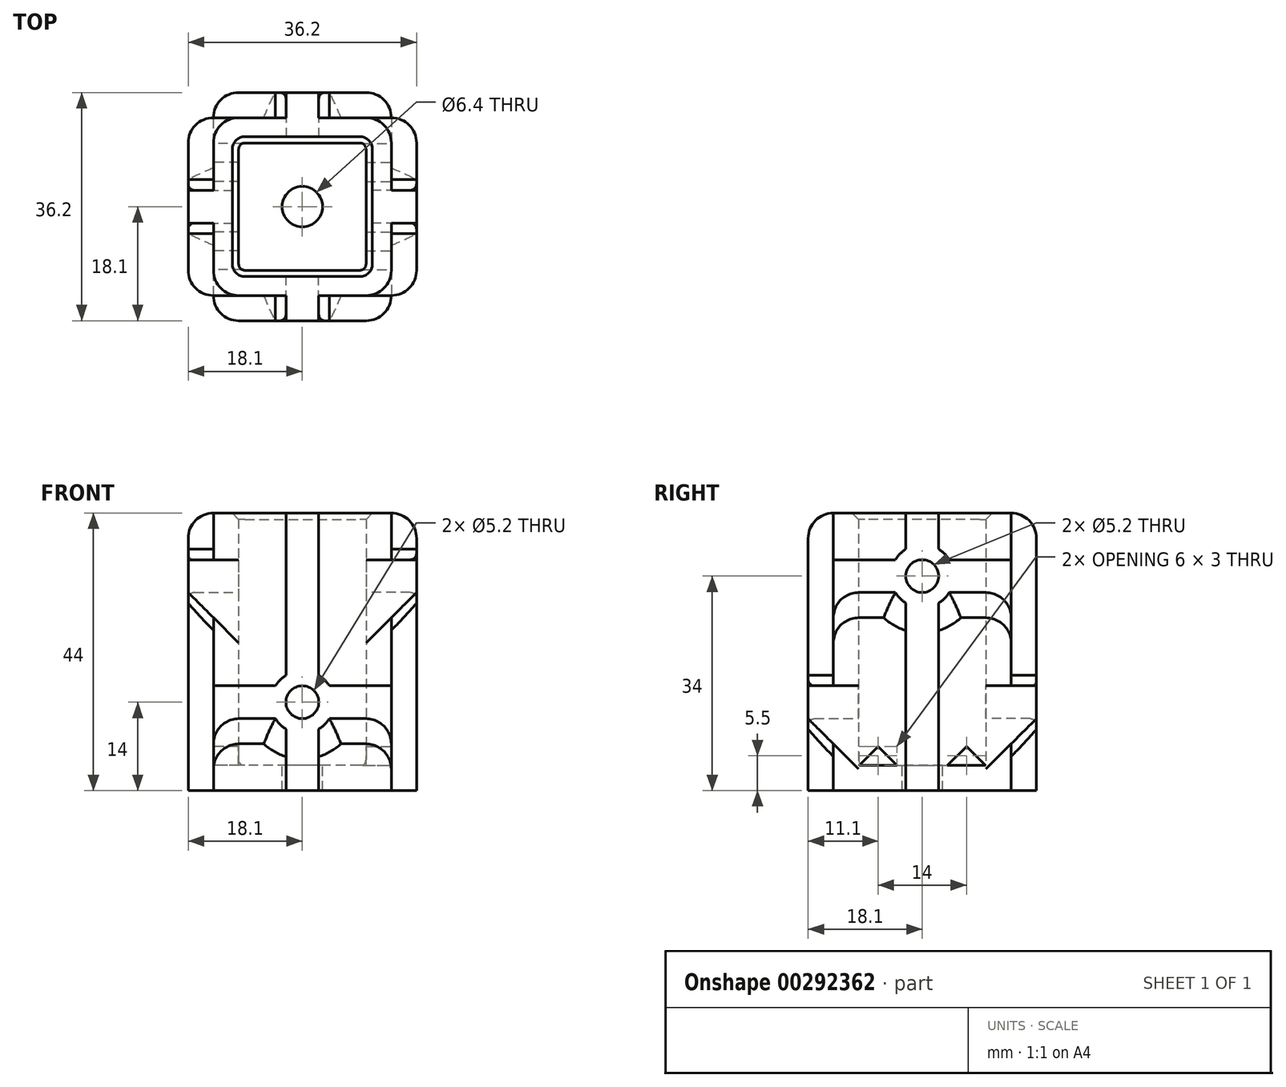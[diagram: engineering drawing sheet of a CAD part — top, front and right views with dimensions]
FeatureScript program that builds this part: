
annotation { "Feature Type Name" : "Feature", "Feature Type Description" : "" }
export const myFeature = defineFeature(function(context is Context, id is Id, definition is map)
    precondition{}
    {
        {
            var Q0;
            Q0=qCreatedBy(makeId("Top.planeOp"),FACE);
            var sketch = newSketch(context, id + "F0", { "sketchPlane" : qUnion([Q0])});
            skLineSegment(sketch, "E0.rect.bottom", {"start": v(10.1, -10.1) * mm, "end": v(-10.1, -10.1) * mm});
            skLineSegment(sketch, "E0.rect.top", {"start": v(10.1, 10.1) * mm, "end": v(-10.1, 10.1) * mm, "construction": true});
            skLineSegment(sketch, "E0.rect.left", {"start": v(10.1, -10.1) * mm, "end": v(10.1, 10.1) * mm, "construction": true});
            skLineSegment(sketch, "E0.rect.right", {"start": v(-10.1, -10.1) * mm, "end": v(-10.1, 10.1) * mm});
            skPoint(sketch, "E0.rect.middle", {"position": v(0, 0) * mm});
            skLineSegment(sketch, "E1.0", {"start": v(14.1, -14.1) * mm, "end": v(14.1, 14.1) * mm, "construction": true});
            skLineSegment(sketch, "E1.1", {"start": v(14.1, -14.1) * mm, "end": v(-14.1, -14.1) * mm});
            skLineSegment(sketch, "E1.2", {"start": v(-14.1, -14.1) * mm, "end": v(-14.1, 14.1) * mm});
            skLineSegment(sketch, "E1.3", {"start": v(14.1, 14.1) * mm, "end": v(-14.1, 14.1) * mm, "construction": true});
            skCircle(sketch, "E2", {"center": v(0, 0) * mm, "radius": 3.2 * mm});
            skLineSegment(sketch, "E3", {"start": v(-14.1, 14.1) * mm, "end": v(-2.26, 2.26) * mm});
            skLineSegment(sketch, "E4", {"start": v(2.26, -2.26) * mm, "end": v(14.1, -14.1) * mm});
            skSolve(sketch);
        }
        {
            var Q0;
            {var subQ5=sQuery(id+"F0.wireOp",EDGE,"E0.rect.right");Q0=makeQuery(id+"F0.imprint","IMPRINT",FACE,{"disambiguationData":[TD([[makeQuery(id+"F0.imprint","IMPRINT",EDGE,{"derivedFrom":subQ5}),1.0]])]});}
            extrude(context, id + "F1", {"entities" : qUnion([Q0]), "depth" : 40 * mm});
        }
        {
            var Q0;
            {var subQ3=sQuery(id+"F0.wireOp",EDGE,"E0.rect.bottom");Q0=makeQuery(id+"F0.imprint","IMPRINT",FACE,{"disambiguationData":[TD([[makeQuery(id+"F0.imprint","IMPRINT",EDGE,{"derivedFrom":subQ3}),1.0]])]});}
            var Q1;
            {var subQ0=sQuery(id+"F0.wireOp",EDGE,"E0.rect.bottom");Q1=makeQuery(id+"F0.imprint","IMPRINT",FACE,{"disambiguationData":[TD([[makeQuery(id+"F0.imprint","IMPRINT",EDGE,{"derivedFrom":subQ0}),-1.0]])]});}
            extrude(context, id + "F2", {"entities" : qUnion([Q0, Q1]), "operationType" : NewBodyOperationType.ADD, "oppositeDirection" : true, "depth" : 4 * mm});
        }
        {
            var Q0;
            Q0=qCreatedBy(makeId("Front.planeOp"),FACE);
            var sketch = newSketch(context, id + "F3", { "sketchPlane" : qUnion([Q0])});
            skCircle(sketch, "E5", {"center": v(0, 10) * mm, "radius": 2.6 * mm});
            skSolve(sketch);
        }
        {
            var Q0;
            Q0=makeQuery(id+"F3.imprint","IMPRINT",FACE,{"disambiguationData":[TD([[makeQuery(id+"F3.imprint","IMPRINT",EDGE,{"derivedFrom":sQuery(id+"F3.wireOp",EDGE,"E5")}),1.0]])]});
            extrude(context, id + "F4", {"entities" : qUnion([Q0]), "operationType" : NewBodyOperationType.REMOVE, "depth" : 25 * mm});
        }
        {
            var Q0;
            Q0=makeQuery(id+"F3.imprint","IMPRINT",FACE,{"disambiguationData":[TD([[makeQuery(id+"F3.imprint","IMPRINT",EDGE,{"derivedFrom":sQuery(id+"F3.wireOp",EDGE,"E5")}),-1.0]])]});
            var Q1;
            Q1=makeQuery(id+"F3.imprint","IMPRINT",FACE,{"disambiguationData":[TD([[makeQuery(id+"F3.imprint","IMPRINT",EDGE,{"derivedFrom":sQuery(id+"F3.wireOp",EDGE,"E5")}),1.0]])]});
            extrude(context, id + "F5", {"entities" : qUnion([Q0, Q1]), "operationType" : NewBodyOperationType.REMOVE, "oppositeDirection" : true, "depth" : 25 * mm});
        }
        {
            var Q0;
            Q0=qCreatedBy(makeId("Right.planeOp"),FACE);
            var sketch = newSketch(context, id + "F6", { "sketchPlane" : qUnion([Q0])});
            skCircle(sketch, "E6", {"center": v(0, 30) * mm, "radius": 2.6 * mm});
            skLineSegment(sketch, "E7", {"start": v(-10, 0) * mm, "end": v(-4, 0) * mm});
            skLineSegment(sketch, "E8", {"start": v(-4, 0) * mm, "end": v(-7, 3) * mm});
            skLineSegment(sketch, "E9", {"start": v(-7, 3) * mm, "end": v(-10, 0) * mm});
            skLineSegment(sketch, "E10", {"start": v(0, 0) * mm, "end": v(0, 30) * mm, "construction": true});
            skLineSegment(sketch, "E11.MirrorCS", {"start": v(10, 0) * mm, "end": v(4, 0) * mm});
            skLineSegment(sketch, "E12.MirrorCS", {"start": v(4, 0) * mm, "end": v(7, 3) * mm});
            skLineSegment(sketch, "E13.MirrorCS", {"start": v(7, 3) * mm, "end": v(10, 0) * mm});
            skSolve(sketch);
        }
        {
            var Q0;
            Q0=makeQuery(id+"F6.imprint","IMPRINT",FACE,{"disambiguationData":[TD([[makeQuery(id+"F6.imprint","IMPRINT",EDGE,{"derivedFrom":sQuery(id+"F6.wireOp",EDGE,"E6")}),1.0]])]});
            var Q1;
            Q1=makeQuery(id+"F6.imprint","IMPRINT",FACE,{"disambiguationData":[TD([[makeQuery(id+"F6.imprint","IMPRINT",EDGE,{"derivedFrom":sQuery(id+"F6.wireOp",EDGE,"f3287db6-100c-4814-bab7-777f2fd4f9ab")}),1.0]])]});
            extrude(context, id + "F7", {"entities" : qUnion([Q0, Q1]), "operationType" : NewBodyOperationType.REMOVE, "endBound" : BoundingType.SYMMETRIC, "oppositeDirection" : true, "depth" : 50 * mm});
        }
        {
            var Q0;
            Q0=makeQuery(id+"F6.imprint","IMPRINT",FACE,{"disambiguationData":[TD([[makeQuery(id+"F6.imprint","IMPRINT",EDGE,{"derivedFrom":sQuery(id+"F6.wireOp",EDGE,"E11.MirrorCS")}),-1.0]])]});
            var Q1;
            Q1=makeQuery(id+"F6.imprint","IMPRINT",FACE,{"disambiguationData":[TD([[makeQuery(id+"F6.imprint","IMPRINT",EDGE,{"derivedFrom":sQuery(id+"F6.wireOp",EDGE,"E7")}),1.0]])]});
            extrude(context, id + "F8", {"entities" : qUnion([Q0, Q1]), "operationType" : NewBodyOperationType.REMOVE, "endBound" : BoundingType.SYMMETRIC, "depth" : 50 * mm});
        }
        {
            var Q0;
            {var subQ0=sQuery(id+"F0.wireOp",EDGE,"E1.1");Q0=makeQuery(id+"F2.boolean.opBoolean","MERGE",FACE,{"derivedFrom":[makeQuery(id+"F9Dm1DlvACU9APN_1.boolean.opBoolean","MERGE",FACE,{"derivedFrom":[makeQuery(id+"F1.opExtrude","SWEPT_FACE",FACE,{"disambiguationData":[OSD([subQ0])]}),makeQuery(id+"F9Dm1DlvACU9APN_1.opExtrude","SWEPT_FACE",FACE,{"disambiguationData":[OSD([subQ0])]})]}),makeQuery(id+"F2.opExtrude","SWEPT_FACE",FACE,{"disambiguationData":[OSD([subQ0])]})]});}
            var sketch = newSketch(context, id + "F9", { "sketchPlane" : qUnion([Q0])});
            skArc(sketch, "E14", {"start": v(-4.27, 7.4) * mm, "mid": v(-3.54, 6.46) * mm, "end": v(-2.6, 5.73) * mm});
            skLineSegment(sketch, "E15.rect.bottom", {"start": v(2.6, 40) * mm, "end": v(-2.6, 40) * mm});
            skLineSegment(sketch, "E15.rect.left", {"start": v(2.6, 40) * mm, "end": v(2.6, 14.27) * mm});
            skLineSegment(sketch, "E15.rect.right", {"start": v(-2.6, 40) * mm, "end": v(-2.6, 14.27) * mm});
            skLineSegment(sketch, "E16.rect.bottom", {"start": v(14.1, 12.6) * mm, "end": v(4.27, 12.6) * mm});
            skLineSegment(sketch, "E16.rect.top", {"start": v(14.1, 7.4) * mm, "end": v(4.27, 7.4) * mm});
            skLineSegment(sketch, "E16.rect.left", {"start": v(14.1, 12.6) * mm, "end": v(14.1, 7.4) * mm});
            skLineSegment(sketch, "E16.rect.right", {"start": v(-14.1, 12.6) * mm, "end": v(-14.1, 7.4) * mm});
            skLineSegment(sketch, "E17.0", {"start": v(2.6, -4) * mm, "end": v(-2.6, -4) * mm});
            skLineSegment(sketch, "E18.trimOffspring", {"start": v(-2.6, 5.73) * mm, "end": v(-2.6, -4) * mm});
            skLineSegment(sketch, "E19.trimOffspring", {"start": v(-4.27, 7.4) * mm, "end": v(-14.1, 7.4) * mm});
            skLineSegment(sketch, "E20.trimOffspring", {"start": v(-4.27, 12.6) * mm, "end": v(-14.1, 12.6) * mm});
            skLineSegment(sketch, "E21.trimOffspring", {"start": v(2.6, 5.73) * mm, "end": v(2.6, -4) * mm});
            skArc(sketch, "E22.trimOffspring", {"start": v(-2.6, 14.27) * mm, "mid": v(-3.54, 13.54) * mm, "end": v(-4.27, 12.6) * mm});
            skArc(sketch, "E23.trimOffspring", {"start": v(4.27, 12.6) * mm, "mid": v(3.54, 13.54) * mm, "end": v(2.6, 14.27) * mm});
            skArc(sketch, "E24.trimOffspring", {"start": v(2.6, 5.73) * mm, "mid": v(3.54, 6.46) * mm, "end": v(4.27, 7.4) * mm});
            skSolve(sketch);
        }
        {
            var Q0;
            {var subQ0=sQuery(id+"F0.wireOp",EDGE,"E1.2");Q0=makeQuery(id+"F2.boolean.opBoolean","MERGE",FACE,{"derivedFrom":[makeQuery(id+"F1.opExtrude","SWEPT_FACE",FACE,{"disambiguationData":[OSD([subQ0])]}),makeQuery(id+"F2.opExtrude","SWEPT_FACE",FACE,{"disambiguationData":[OSD([subQ0])]})]});}
            var sketch = newSketch(context, id + "F10", { "sketchPlane" : qUnion([Q0])});
            skArc(sketch, "E25", {"start": v(-4.27, 27.4) * mm, "mid": v(-3.54, 26.46) * mm, "end": v(-2.6, 25.73) * mm});
            skLineSegment(sketch, "E26.rect.bottom", {"start": v(2.6, -4) * mm, "end": v(-2.6, -4) * mm});
            skLineSegment(sketch, "E26.rect.left", {"start": v(2.6, -4) * mm, "end": v(2.6, 25.73) * mm});
            skLineSegment(sketch, "E26.rect.right", {"start": v(-2.6, -4) * mm, "end": v(-2.6, 25.73) * mm});
            skLineSegment(sketch, "E27.0", {"start": v(2.6, 40) * mm, "end": v(-2.6, 40) * mm});
            skLineSegment(sketch, "E28.rect.bottom", {"start": v(14.1, 32.6) * mm, "end": v(4.27, 32.6) * mm});
            skLineSegment(sketch, "E28.rect.top", {"start": v(14.1, 27.4) * mm, "end": v(4.27, 27.4) * mm});
            skLineSegment(sketch, "E28.rect.left", {"start": v(14.1, 32.6) * mm, "end": v(14.1, 27.4) * mm});
            skLineSegment(sketch, "E28.rect.right", {"start": v(-14.1, 32.6) * mm, "end": v(-14.1, 27.4) * mm});
            skLineSegment(sketch, "E29.trimOffspring", {"start": v(-4.27, 32.6) * mm, "end": v(-14.1, 32.6) * mm});
            skLineSegment(sketch, "E30.trimOffspring", {"start": v(-2.6, 34.27) * mm, "end": v(-2.6, 40) * mm});
            skLineSegment(sketch, "E31.trimOffspring", {"start": v(2.6, 34.27) * mm, "end": v(2.6, 40) * mm});
            skLineSegment(sketch, "E32.trimOffspring", {"start": v(-4.27, 27.4) * mm, "end": v(-14.1, 27.4) * mm});
            skArc(sketch, "E33.trimOffspring", {"start": v(-2.6, 34.27) * mm, "mid": v(-3.54, 33.54) * mm, "end": v(-4.27, 32.6) * mm});
            skArc(sketch, "E34.trimOffspring", {"start": v(4.27, 32.6) * mm, "mid": v(3.54, 33.54) * mm, "end": v(2.6, 34.27) * mm});
            skArc(sketch, "E35.trimOffspring", {"start": v(2.6, 25.73) * mm, "mid": v(3.54, 26.46) * mm, "end": v(4.27, 27.4) * mm});
            skSolve(sketch);
        }
        {
            var Q0;
            Q0=makeQuery(id+"F9.imprint","IMPRINT",FACE,{"disambiguationData":[TD([[makeQuery(id+"F9.imprint","IMPRINT",EDGE,{"derivedFrom":sQuery(id+"F9.wireOp",EDGE,"E14")}),1.0]])]});
            extrude(context, id + "F11", {"entities" : qUnion([Q0]), "operationType" : NewBodyOperationType.ADD, "depth" : 4 * mm});
        }
        {
            var Q0;
            Q0=makeQuery(id+"F11.opExtrude","CAP_EDGE",EDGE,{"disambiguationData":[OSD([sQuery(id+"F9.wireOp",EDGE,"E14")])],"isStart":true});
            var Q1;
            Q1=makeQuery(id+"F11.opExtrude","CAP_EDGE",EDGE,{"disambiguationData":[OSD([sQuery(id+"F9.wireOp",EDGE,"E24.trimOffspring")])],"isStart":true});
            var Q2;
            Q2=makeQuery(id+"F11.opExtrude","CAP_EDGE",EDGE,{"disambiguationData":[OSD([sQuery(id+"F9.wireOp",EDGE,"E16.rect.top")])],"isStart":true});
            var Q3;
            Q3=makeQuery(id+"F11.opExtrude","CAP_EDGE",EDGE,{"disambiguationData":[OSD([sQuery(id+"F9.wireOp",EDGE,"E19.trimOffspring")])],"isStart":true});
            chamfer(context, id + "F12", {"entities" : qUnion([Q0, Q1, Q2, Q3]), "width" : 4 * mm, "tangentPropagation" : true});
        }
        {
            var Q0;
            Q0=makeQuery(id+"F10.imprint","IMPRINT",FACE,{"disambiguationData":[TD([[makeQuery(id+"F10.imprint","IMPRINT",EDGE,{"derivedFrom":sQuery(id+"F10.wireOp",EDGE,"E25")}),1.0]])]});
            extrude(context, id + "F13", {"entities" : qUnion([Q0]), "operationType" : NewBodyOperationType.ADD, "depth" : 4 * mm});
        }
        {
            var Q0;
            Q0=makeQuery(id+"F13.opExtrude","CAP_EDGE",EDGE,{"disambiguationData":[OSD([sQuery(id+"F10.wireOp",EDGE,"E25")])],"isStart":true});
            var Q1;
            Q1=makeQuery(id+"F13.opExtrude","CAP_EDGE",EDGE,{"disambiguationData":[OSD([sQuery(id+"F10.wireOp",EDGE,"E32.trimOffspring")])],"isStart":true});
            var Q2;
            Q2=makeQuery(id+"F13.opExtrude","CAP_EDGE",EDGE,{"disambiguationData":[OSD([sQuery(id+"F10.wireOp",EDGE,"E35.trimOffspring")])],"isStart":true});
            var Q3;
            Q3=makeQuery(id+"F13.opExtrude","CAP_EDGE",EDGE,{"disambiguationData":[OSD([sQuery(id+"F10.wireOp",EDGE,"E28.rect.top")])],"isStart":true});
            chamfer(context, id + "F14", {"entities" : qUnion([Q0, Q1, Q2, Q3]), "width" : 4 * mm, "tangentPropagation" : true});
        }
        {
            var Q0;
            Q0=makeQuery(id+"F1.opExtrude","SWEPT_BODY",BODY,{"disambiguationData":[OSD([sQuery(id+"F0.wireOp",EDGE,"E0.rect.bottom"),sQuery(id+"F0.wireOp",EDGE,"E0.rect.right"),sQuery(id+"F0.wireOp",EDGE,"E1.1"),sQuery(id+"F0.wireOp",EDGE,"E1.2"),sQuery(id+"F0.wireOp",EDGE,"E3"),sQuery(id+"F0.wireOp",EDGE,"E4")])]});
            var Q1;
            {var subQ0=sQuery(id+"F0.wireOp",EDGE,"E3");Q1=makeQuery(id+"F2.boolean.opBoolean","MERGE",FACE,{"derivedFrom":[makeQuery(id+"F1.opExtrude","SWEPT_FACE",FACE,{"disambiguationData":[OSD([subQ0])]}),makeQuery(id+"F2.opExtrude","SWEPT_FACE",FACE,{"disambiguationData":[OSD([subQ0])]})]});}
            mirror(context, id + "F15", {"entities" : qUnion([Q0]), "mirrorPlane" : qUnion([Q1])});
        }
        {
            var Q0;
            Q0=makeQuery(id+"F15.opPattern","COPY",VERTEX,{"derivedFrom":makeQuery(id+"F1.opExtrude","CAP_VERTEX",VERTEX,{"disambiguationData":[OSD([sQuery(id+"F0.wireOp",EDGE,"E1.1"),sQuery(id+"F0.wireOp",EDGE,"E1.2")])],"isStart":false}),"instanceName":"1"});
            var Q1;
            Q1=makeQuery(id+"F1.opExtrude","CAP_VERTEX",VERTEX,{"disambiguationData":[OSD([sQuery(id+"F0.wireOp",EDGE,"E1.1"),sQuery(id+"F0.wireOp",EDGE,"E1.2")])],"isStart":false});
            var Q2;
            Q2=makeQuery(id+"F2.opExtrude","CAP_VERTEX",VERTEX,{"disambiguationData":[OSD([sQuery(id+"F0.wireOp",EDGE,"E1.1"),sQuery(id+"F0.wireOp",EDGE,"E1.2")])],"isStart":false});
            cPlane(context, id + "F16", {"entities" : qUnion([Q0, Q1, Q2]), "cplaneType" : CPlaneType.THREE_POINT, "offset" : 0 * mm, "width" : 150 * mm, "height" : 150 * mm});
        }
        {
            var Q0;
            Q0=makeQuery(id+"F15.opPattern","COPY",BODY,{"derivedFrom":makeQuery(id+"F1.opExtrude","SWEPT_BODY",BODY,{"disambiguationData":[OSD([sQuery(id+"F0.wireOp",EDGE,"E0.rect.bottom"),sQuery(id+"F0.wireOp",EDGE,"E0.rect.right"),sQuery(id+"F0.wireOp",EDGE,"E1.1"),sQuery(id+"F0.wireOp",EDGE,"E1.2"),sQuery(id+"F0.wireOp",EDGE,"E3"),sQuery(id+"F0.wireOp",EDGE,"E4")])]}),"instanceName":"1"});
            var Q1;
            Q1=qCreatedBy(id+"F16.planeOp",FACE);
            mirror(context, id + "F17", {"entities" : qUnion([Q0]), "mirrorPlane" : qUnion([Q1])});
        }
        {
            var Q0;
            Q0=makeQuery(id+"F15.opPattern","COPY",BODY,{"derivedFrom":makeQuery(id+"F1.opExtrude","SWEPT_BODY",BODY,{"disambiguationData":[OSD([sQuery(id+"F0.wireOp",EDGE,"E0.rect.bottom"),sQuery(id+"F0.wireOp",EDGE,"E0.rect.right"),sQuery(id+"F0.wireOp",EDGE,"E1.1"),sQuery(id+"F0.wireOp",EDGE,"E1.2"),sQuery(id+"F0.wireOp",EDGE,"E3"),sQuery(id+"F0.wireOp",EDGE,"E4")])]}),"instanceName":"1"});
            deleteBodies(context, id + "F18", {"entities" : qUnion([Q0])});
        }
        {
            var Q0;
            Q0=makeQuery(id+"F1.opExtrude","SWEPT_BODY",BODY,{"disambiguationData":[OSD([sQuery(id+"F0.wireOp",EDGE,"E0.rect.bottom"),sQuery(id+"F0.wireOp",EDGE,"E0.rect.right"),sQuery(id+"F0.wireOp",EDGE,"E1.1"),sQuery(id+"F0.wireOp",EDGE,"E1.2"),sQuery(id+"F0.wireOp",EDGE,"E3"),sQuery(id+"F0.wireOp",EDGE,"E4")])]});
            var Q1;
            Q1=makeQuery(id+"F17.opPattern","COPY",BODY,{"derivedFrom":makeQuery(id+"F15.opPattern","COPY",BODY,{"derivedFrom":makeQuery(id+"F1.opExtrude","SWEPT_BODY",BODY,{"disambiguationData":[OSD([sQuery(id+"F0.wireOp",EDGE,"E0.rect.bottom"),sQuery(id+"F0.wireOp",EDGE,"E0.rect.right"),sQuery(id+"F0.wireOp",EDGE,"E1.1"),sQuery(id+"F0.wireOp",EDGE,"E1.2"),sQuery(id+"F0.wireOp",EDGE,"E3"),sQuery(id+"F0.wireOp",EDGE,"E4")])]}),"instanceName":"1"}),"instanceName":"1"});
            booleanBodies(context, id + "F19", {"operationType" : BooleanOperationType.UNION, "tools" : qUnion([Q0, Q1])});
        }
        {
            var Q0;
            Q0=makeQuery(id+"F19.opBoolean","MERGE",EDGE,{"derivedFrom":[makeQuery(id+"F1.opExtrude","SWEPT_EDGE",EDGE,{"disambiguationData":[OSD([sQuery(id+"F0.wireOp",EDGE,"E0.rect.bottom"),sQuery(id+"F0.wireOp",EDGE,"E4")])]}),makeQuery(id+"F17.opPattern","COPY",EDGE,{"derivedFrom":makeQuery(id+"F15.opPattern","COPY",EDGE,{"derivedFrom":makeQuery(id+"F1.opExtrude","SWEPT_EDGE",EDGE,{"disambiguationData":[OSD([sQuery(id+"F0.wireOp",EDGE,"E0.rect.right"),sQuery(id+"F0.wireOp",EDGE,"E3")])]}),"instanceName":"1"}),"instanceName":"1"})]});
            var Q1;
            Q1=makeQuery(id+"F1.opExtrude","SWEPT_EDGE",EDGE,{"disambiguationData":[OSD([sQuery(id+"F0.wireOp",EDGE,"E0.rect.bottom"),sQuery(id+"F0.wireOp",EDGE,"E0.rect.right")])]});
            var Q2;
            Q2=makeQuery(id+"F19.opBoolean","MERGE",EDGE,{"derivedFrom":[makeQuery(id+"F1.opExtrude","SWEPT_EDGE",EDGE,{"disambiguationData":[OSD([sQuery(id+"F0.wireOp",EDGE,"E0.rect.right"),sQuery(id+"F0.wireOp",EDGE,"E3")])]}),makeQuery(id+"F17.opPattern","COPY",EDGE,{"derivedFrom":makeQuery(id+"F15.opPattern","COPY",EDGE,{"derivedFrom":makeQuery(id+"F1.opExtrude","SWEPT_EDGE",EDGE,{"disambiguationData":[OSD([sQuery(id+"F0.wireOp",EDGE,"E0.rect.bottom"),sQuery(id+"F0.wireOp",EDGE,"E4")])]}),"instanceName":"1"}),"instanceName":"1"})]});
            var Q3;
            Q3=makeQuery(id+"F17.opPattern","COPY",EDGE,{"derivedFrom":makeQuery(id+"F15.opPattern","COPY",EDGE,{"derivedFrom":makeQuery(id+"F1.opExtrude","SWEPT_EDGE",EDGE,{"disambiguationData":[OSD([sQuery(id+"F0.wireOp",EDGE,"E0.rect.bottom"),sQuery(id+"F0.wireOp",EDGE,"E0.rect.right")])]}),"instanceName":"1"}),"instanceName":"1"});
            fillet(context, id + "F20", {"entities" : qUnion([Q0, Q1, Q2, Q3]), "radius" : 1 * mm, "tangentPropagation" : true, "allowEdgeOverflow" : false});
        }
        {
            var Q0;
            {var subQ0=sQuery(id+"F0.wireOp",EDGE,"E1.1");var subQ1=sQuery(id+"F0.wireOp",EDGE,"E1.2");var subQ2=makeQuery(id+"F11.opExtrude","SWEPT_FACE",FACE,{"disambiguationData":[OSD([sQuery(id+"F9.wireOp",EDGE,"E15.rect.bottom")])]});Q0=makeQuery(id+"F13.boolean.opBoolean","SPLIT",EDGE,{"disambiguationData":[TD([subQ2])],"derivedFrom":makeQuery(id+"F11.boolean.opBoolean","SPLIT",EDGE,{"disambiguationData":[TD([subQ2])],"derivedFrom":makeQuery(id+"F2.boolean.opBoolean","MERGE",EDGE,{"derivedFrom":[makeQuery(id+"F1.opExtrude","SWEPT_EDGE",EDGE,{"disambiguationData":[OSD([subQ0,subQ1])]}),makeQuery(id+"F2.opExtrude","SWEPT_EDGE",EDGE,{"disambiguationData":[OSD([subQ0,subQ1])]})]})})});}
            var Q1;
            {var subQ0=sQuery(id+"F0.wireOp",EDGE,"E1.1");var subQ1=sQuery(id+"F0.wireOp",EDGE,"E1.2");var subQ2=makeQuery(id+"F11.opExtrude","SWEPT_FACE",FACE,{"disambiguationData":[OSD([sQuery(id+"F9.wireOp",EDGE,"E20.trimOffspring")])]});Q1=makeQuery(id+"F13.boolean.opBoolean","SPLIT",EDGE,{"disambiguationData":[TD([subQ2])],"derivedFrom":makeQuery(id+"F11.boolean.opBoolean","SPLIT",EDGE,{"disambiguationData":[TD([makeQuery(id+"F11.opExtrude","SWEPT_FACE",FACE,{"disambiguationData":[OSD([sQuery(id+"F9.wireOp",EDGE,"E15.rect.bottom")])]})])],"derivedFrom":makeQuery(id+"F2.boolean.opBoolean","MERGE",EDGE,{"derivedFrom":[makeQuery(id+"F1.opExtrude","SWEPT_EDGE",EDGE,{"disambiguationData":[OSD([subQ0,subQ1])]}),makeQuery(id+"F2.opExtrude","SWEPT_EDGE",EDGE,{"disambiguationData":[OSD([subQ0,subQ1])]})]})})});}
            var Q2;
            {var subQ0=sQuery(id+"F0.wireOp",EDGE,"E1.1");var subQ1=sQuery(id+"F0.wireOp",EDGE,"E1.2");Q2=makeQuery(id+"F11.boolean.opBoolean","SPLIT",EDGE,{"disambiguationData":[TD([makeQuery(id+"F11.opExtrude","SWEPT_FACE",FACE,{"disambiguationData":[OSD([sQuery(id+"F9.wireOp",EDGE,"E17.0")])]})])],"derivedFrom":makeQuery(id+"F2.boolean.opBoolean","MERGE",EDGE,{"derivedFrom":[makeQuery(id+"F1.opExtrude","SWEPT_EDGE",EDGE,{"disambiguationData":[OSD([subQ0,subQ1])]}),makeQuery(id+"F2.opExtrude","SWEPT_EDGE",EDGE,{"disambiguationData":[OSD([subQ0,subQ1])]})]})});}
            var Q3;
            {var subQ0=sQuery(id+"F0.wireOp",EDGE,"E1.2");var subQ1=sQuery(id+"F0.wireOp",EDGE,"E3");var subQ2=makeQuery(id+"F11.opExtrude","SWEPT_FACE",FACE,{"disambiguationData":[OSD([sQuery(id+"F9.wireOp",EDGE,"E15.rect.bottom")])]});var subQ3=sQuery(id+"F0.wireOp",EDGE,"E1.1");var subQ4=sQuery(id+"F0.wireOp",EDGE,"E4");Q3=makeQuery(id+"F19.opBoolean","MERGE",EDGE,{"derivedFrom":[makeQuery(id+"F13.boolean.opBoolean","SPLIT",EDGE,{"disambiguationData":[TD([subQ2])],"derivedFrom":makeQuery(id+"F2.boolean.opBoolean","MERGE",EDGE,{"derivedFrom":[makeQuery(id+"F1.opExtrude","SWEPT_EDGE",EDGE,{"disambiguationData":[OSD([subQ0,subQ1])]}),makeQuery(id+"F2.opExtrude","SWEPT_EDGE",EDGE,{"disambiguationData":[OSD([subQ0,subQ1])]})]})}),makeQuery(id+"F17.opPattern","COPY",EDGE,{"derivedFrom":makeQuery(id+"F15.opPattern","COPY",EDGE,{"derivedFrom":makeQuery(id+"F11.boolean.opBoolean","SPLIT",EDGE,{"disambiguationData":[TD([subQ2])],"derivedFrom":makeQuery(id+"F2.boolean.opBoolean","MERGE",EDGE,{"derivedFrom":[makeQuery(id+"F1.opExtrude","SWEPT_EDGE",EDGE,{"disambiguationData":[OSD([subQ3,subQ4])]}),makeQuery(id+"F2.opExtrude","SWEPT_EDGE",EDGE,{"disambiguationData":[OSD([subQ3,subQ4])]})]})}),"instanceName":"1"}),"instanceName":"1"})]});}
            var Q4;
            {var subQ0=sQuery(id+"F0.wireOp",EDGE,"E1.2");var subQ1=sQuery(id+"F0.wireOp",EDGE,"E3");var subQ2=sQuery(id+"F0.wireOp",EDGE,"E1.1");var subQ3=sQuery(id+"F0.wireOp",EDGE,"E4");Q4=makeQuery(id+"F19.opBoolean","MERGE",EDGE,{"derivedFrom":[makeQuery(id+"F13.boolean.opBoolean","SPLIT",EDGE,{"disambiguationData":[TD([makeQuery(id+"F11.opExtrude","SWEPT_FACE",FACE,{"disambiguationData":[OSD([sQuery(id+"F9.wireOp",EDGE,"E17.0")])]})])],"derivedFrom":makeQuery(id+"F2.boolean.opBoolean","MERGE",EDGE,{"derivedFrom":[makeQuery(id+"F1.opExtrude","SWEPT_EDGE",EDGE,{"disambiguationData":[OSD([subQ0,subQ1])]}),makeQuery(id+"F2.opExtrude","SWEPT_EDGE",EDGE,{"disambiguationData":[OSD([subQ0,subQ1])]})]})}),makeQuery(id+"F17.opPattern","COPY",EDGE,{"derivedFrom":makeQuery(id+"F15.opPattern","COPY",EDGE,{"derivedFrom":makeQuery(id+"F11.boolean.opBoolean","SPLIT",EDGE,{"disambiguationData":[TD([makeQuery(id+"F11.opExtrude","SWEPT_FACE",FACE,{"disambiguationData":[OSD([sQuery(id+"F9.wireOp",EDGE,"E15.rect.bottom")])]})])],"derivedFrom":makeQuery(id+"F2.boolean.opBoolean","MERGE",EDGE,{"derivedFrom":[makeQuery(id+"F1.opExtrude","SWEPT_EDGE",EDGE,{"disambiguationData":[OSD([subQ2,subQ3])]}),makeQuery(id+"F2.opExtrude","SWEPT_EDGE",EDGE,{"disambiguationData":[OSD([subQ2,subQ3])]})]})}),"instanceName":"1"}),"instanceName":"1"})]});}
            var Q5;
            {var subQ0=sQuery(id+"F0.wireOp",EDGE,"E1.2");var subQ1=sQuery(id+"F0.wireOp",EDGE,"E3");var subQ2=makeQuery(id+"F11.opExtrude","SWEPT_FACE",FACE,{"disambiguationData":[OSD([sQuery(id+"F9.wireOp",EDGE,"E17.0")])]});var subQ3=sQuery(id+"F0.wireOp",EDGE,"E1.1");var subQ4=sQuery(id+"F0.wireOp",EDGE,"E4");Q5=makeQuery(id+"F19.opBoolean","MERGE",EDGE,{"derivedFrom":[makeQuery(id+"F13.boolean.opBoolean","SPLIT",EDGE,{"disambiguationData":[TD([subQ2])],"derivedFrom":makeQuery(id+"F2.boolean.opBoolean","MERGE",EDGE,{"derivedFrom":[makeQuery(id+"F1.opExtrude","SWEPT_EDGE",EDGE,{"disambiguationData":[OSD([subQ0,subQ1])]}),makeQuery(id+"F2.opExtrude","SWEPT_EDGE",EDGE,{"disambiguationData":[OSD([subQ0,subQ1])]})]})}),makeQuery(id+"F17.opPattern","COPY",EDGE,{"derivedFrom":makeQuery(id+"F15.opPattern","COPY",EDGE,{"derivedFrom":makeQuery(id+"F11.boolean.opBoolean","SPLIT",EDGE,{"disambiguationData":[TD([makeQuery(id+"F11.opExtrude","SWEPT_FACE",FACE,{"disambiguationData":[OSD([sQuery(id+"F9.wireOp",EDGE,"E16.rect.top")])]})])],"derivedFrom":makeQuery(id+"F2.boolean.opBoolean","MERGE",EDGE,{"derivedFrom":[makeQuery(id+"F1.opExtrude","SWEPT_EDGE",EDGE,{"disambiguationData":[OSD([subQ3,subQ4])]}),makeQuery(id+"F2.opExtrude","SWEPT_EDGE",EDGE,{"disambiguationData":[OSD([subQ3,subQ4])]})]})}),"instanceName":"1"}),"instanceName":"1"})]});}
            var Q6;
            {var subQ0=sQuery(id+"F0.wireOp",EDGE,"E1.1");var subQ1=sQuery(id+"F0.wireOp",EDGE,"E1.2");Q6=makeQuery(id+"F17.opPattern","COPY",EDGE,{"derivedFrom":makeQuery(id+"F15.opPattern","COPY",EDGE,{"derivedFrom":makeQuery(id+"F11.boolean.opBoolean","SPLIT",EDGE,{"disambiguationData":[TD([makeQuery(id+"F11.opExtrude","SWEPT_FACE",FACE,{"disambiguationData":[OSD([sQuery(id+"F9.wireOp",EDGE,"E17.0")])]})])],"derivedFrom":makeQuery(id+"F2.boolean.opBoolean","MERGE",EDGE,{"derivedFrom":[makeQuery(id+"F1.opExtrude","SWEPT_EDGE",EDGE,{"disambiguationData":[OSD([subQ0,subQ1])]}),makeQuery(id+"F2.opExtrude","SWEPT_EDGE",EDGE,{"disambiguationData":[OSD([subQ0,subQ1])]})]})}),"instanceName":"1"}),"instanceName":"1"});}
            var Q7;
            {var subQ0=sQuery(id+"F0.wireOp",EDGE,"E1.1");var subQ1=sQuery(id+"F0.wireOp",EDGE,"E1.2");var subQ2=makeQuery(id+"F11.opExtrude","SWEPT_FACE",FACE,{"disambiguationData":[OSD([sQuery(id+"F9.wireOp",EDGE,"E20.trimOffspring")])]});Q7=makeQuery(id+"F17.opPattern","COPY",EDGE,{"derivedFrom":makeQuery(id+"F15.opPattern","COPY",EDGE,{"derivedFrom":makeQuery(id+"F13.boolean.opBoolean","SPLIT",EDGE,{"disambiguationData":[TD([subQ2])],"derivedFrom":makeQuery(id+"F11.boolean.opBoolean","SPLIT",EDGE,{"disambiguationData":[TD([makeQuery(id+"F11.opExtrude","SWEPT_FACE",FACE,{"disambiguationData":[OSD([sQuery(id+"F9.wireOp",EDGE,"E15.rect.bottom")])]})])],"derivedFrom":makeQuery(id+"F2.boolean.opBoolean","MERGE",EDGE,{"derivedFrom":[makeQuery(id+"F1.opExtrude","SWEPT_EDGE",EDGE,{"disambiguationData":[OSD([subQ0,subQ1])]}),makeQuery(id+"F2.opExtrude","SWEPT_EDGE",EDGE,{"disambiguationData":[OSD([subQ0,subQ1])]})]})})}),"instanceName":"1"}),"instanceName":"1"});}
            var Q8;
            {var subQ0=sQuery(id+"F0.wireOp",EDGE,"E1.1");var subQ1=sQuery(id+"F0.wireOp",EDGE,"E1.2");var subQ2=makeQuery(id+"F11.opExtrude","SWEPT_FACE",FACE,{"disambiguationData":[OSD([sQuery(id+"F9.wireOp",EDGE,"E15.rect.bottom")])]});Q8=makeQuery(id+"F17.opPattern","COPY",EDGE,{"derivedFrom":makeQuery(id+"F15.opPattern","COPY",EDGE,{"derivedFrom":makeQuery(id+"F13.boolean.opBoolean","SPLIT",EDGE,{"disambiguationData":[TD([subQ2])],"derivedFrom":makeQuery(id+"F11.boolean.opBoolean","SPLIT",EDGE,{"disambiguationData":[TD([subQ2])],"derivedFrom":makeQuery(id+"F2.boolean.opBoolean","MERGE",EDGE,{"derivedFrom":[makeQuery(id+"F1.opExtrude","SWEPT_EDGE",EDGE,{"disambiguationData":[OSD([subQ0,subQ1])]}),makeQuery(id+"F2.opExtrude","SWEPT_EDGE",EDGE,{"disambiguationData":[OSD([subQ0,subQ1])]})]})})}),"instanceName":"1"}),"instanceName":"1"});}
            var Q9;
            {var subQ0=sQuery(id+"F0.wireOp",EDGE,"E1.1");var subQ1=sQuery(id+"F0.wireOp",EDGE,"E4");var subQ2=makeQuery(id+"F11.opExtrude","SWEPT_FACE",FACE,{"disambiguationData":[OSD([sQuery(id+"F9.wireOp",EDGE,"E15.rect.bottom")])]});var subQ3=sQuery(id+"F0.wireOp",EDGE,"E1.2");var subQ4=sQuery(id+"F0.wireOp",EDGE,"E3");Q9=makeQuery(id+"F19.opBoolean","MERGE",EDGE,{"derivedFrom":[makeQuery(id+"F11.boolean.opBoolean","SPLIT",EDGE,{"disambiguationData":[TD([subQ2])],"derivedFrom":makeQuery(id+"F2.boolean.opBoolean","MERGE",EDGE,{"derivedFrom":[makeQuery(id+"F1.opExtrude","SWEPT_EDGE",EDGE,{"disambiguationData":[OSD([subQ0,subQ1])]}),makeQuery(id+"F2.opExtrude","SWEPT_EDGE",EDGE,{"disambiguationData":[OSD([subQ0,subQ1])]})]})}),makeQuery(id+"F17.opPattern","COPY",EDGE,{"derivedFrom":makeQuery(id+"F15.opPattern","COPY",EDGE,{"derivedFrom":makeQuery(id+"F13.boolean.opBoolean","SPLIT",EDGE,{"disambiguationData":[TD([subQ2])],"derivedFrom":makeQuery(id+"F2.boolean.opBoolean","MERGE",EDGE,{"derivedFrom":[makeQuery(id+"F1.opExtrude","SWEPT_EDGE",EDGE,{"disambiguationData":[OSD([subQ3,subQ4])]}),makeQuery(id+"F2.opExtrude","SWEPT_EDGE",EDGE,{"disambiguationData":[OSD([subQ3,subQ4])]})]})}),"instanceName":"1"}),"instanceName":"1"})]});}
            var Q10;
            {var subQ0=sQuery(id+"F0.wireOp",EDGE,"E1.1");var subQ1=sQuery(id+"F0.wireOp",EDGE,"E4");var subQ2=sQuery(id+"F0.wireOp",EDGE,"E1.2");var subQ3=sQuery(id+"F0.wireOp",EDGE,"E3");Q10=makeQuery(id+"F19.opBoolean","MERGE",EDGE,{"derivedFrom":[makeQuery(id+"F11.boolean.opBoolean","SPLIT",EDGE,{"disambiguationData":[TD([makeQuery(id+"F11.opExtrude","SWEPT_FACE",FACE,{"disambiguationData":[OSD([sQuery(id+"F9.wireOp",EDGE,"E15.rect.bottom")])]})])],"derivedFrom":makeQuery(id+"F2.boolean.opBoolean","MERGE",EDGE,{"derivedFrom":[makeQuery(id+"F1.opExtrude","SWEPT_EDGE",EDGE,{"disambiguationData":[OSD([subQ0,subQ1])]}),makeQuery(id+"F2.opExtrude","SWEPT_EDGE",EDGE,{"disambiguationData":[OSD([subQ0,subQ1])]})]})}),makeQuery(id+"F17.opPattern","COPY",EDGE,{"derivedFrom":makeQuery(id+"F15.opPattern","COPY",EDGE,{"derivedFrom":makeQuery(id+"F13.boolean.opBoolean","SPLIT",EDGE,{"disambiguationData":[TD([makeQuery(id+"F11.opExtrude","SWEPT_FACE",FACE,{"disambiguationData":[OSD([sQuery(id+"F9.wireOp",EDGE,"E17.0")])]})])],"derivedFrom":makeQuery(id+"F2.boolean.opBoolean","MERGE",EDGE,{"derivedFrom":[makeQuery(id+"F1.opExtrude","SWEPT_EDGE",EDGE,{"disambiguationData":[OSD([subQ2,subQ3])]}),makeQuery(id+"F2.opExtrude","SWEPT_EDGE",EDGE,{"disambiguationData":[OSD([subQ2,subQ3])]})]})}),"instanceName":"1"}),"instanceName":"1"})]});}
            var Q11;
            {var subQ0=sQuery(id+"F0.wireOp",EDGE,"E1.1");var subQ1=sQuery(id+"F0.wireOp",EDGE,"E4");var subQ2=makeQuery(id+"F11.opExtrude","SWEPT_FACE",FACE,{"disambiguationData":[OSD([sQuery(id+"F9.wireOp",EDGE,"E17.0")])]});var subQ3=sQuery(id+"F0.wireOp",EDGE,"E1.2");var subQ4=sQuery(id+"F0.wireOp",EDGE,"E3");Q11=makeQuery(id+"F19.opBoolean","MERGE",EDGE,{"derivedFrom":[makeQuery(id+"F11.boolean.opBoolean","SPLIT",EDGE,{"disambiguationData":[TD([makeQuery(id+"F11.opExtrude","SWEPT_FACE",FACE,{"disambiguationData":[OSD([sQuery(id+"F9.wireOp",EDGE,"E16.rect.top")])]})])],"derivedFrom":makeQuery(id+"F2.boolean.opBoolean","MERGE",EDGE,{"derivedFrom":[makeQuery(id+"F1.opExtrude","SWEPT_EDGE",EDGE,{"disambiguationData":[OSD([subQ0,subQ1])]}),makeQuery(id+"F2.opExtrude","SWEPT_EDGE",EDGE,{"disambiguationData":[OSD([subQ0,subQ1])]})]})}),makeQuery(id+"F17.opPattern","COPY",EDGE,{"derivedFrom":makeQuery(id+"F15.opPattern","COPY",EDGE,{"derivedFrom":makeQuery(id+"F13.boolean.opBoolean","SPLIT",EDGE,{"disambiguationData":[TD([subQ2])],"derivedFrom":makeQuery(id+"F2.boolean.opBoolean","MERGE",EDGE,{"derivedFrom":[makeQuery(id+"F1.opExtrude","SWEPT_EDGE",EDGE,{"disambiguationData":[OSD([subQ3,subQ4])]}),makeQuery(id+"F2.opExtrude","SWEPT_EDGE",EDGE,{"disambiguationData":[OSD([subQ3,subQ4])]})]})}),"instanceName":"1"}),"instanceName":"1"})]});}
            var Q12;
            Q12=makeQuery(id+"F13.opExtrude","CAP_EDGE",EDGE,{"disambiguationData":[OSD([sQuery(id+"F10.wireOp",EDGE,"E28.rect.right")])],"isStart":false});
            var Q13;
            Q13=makeQuery(id+"F17.opPattern","COPY",EDGE,{"derivedFrom":makeQuery(id+"F15.opPattern","COPY",EDGE,{"derivedFrom":makeQuery(id+"F11.opExtrude","CAP_EDGE",EDGE,{"disambiguationData":[OSD([sQuery(id+"F9.wireOp",EDGE,"E16.rect.left")])],"isStart":false}),"instanceName":"1"}),"instanceName":"1"});
            var Q14;
            Q14=makeQuery(id+"F17.opPattern","COPY",EDGE,{"derivedFrom":makeQuery(id+"F15.opPattern","COPY",EDGE,{"derivedFrom":makeQuery(id+"F13.opExtrude","CAP_EDGE",EDGE,{"disambiguationData":[OSD([sQuery(id+"F10.wireOp",EDGE,"E28.rect.left")])],"isStart":false}),"instanceName":"1"}),"instanceName":"1"});
            var Q15;
            Q15=makeQuery(id+"F17.opPattern","COPY",EDGE,{"derivedFrom":makeQuery(id+"F15.opPattern","COPY",EDGE,{"derivedFrom":makeQuery(id+"F11.opExtrude","CAP_EDGE",EDGE,{"disambiguationData":[OSD([sQuery(id+"F9.wireOp",EDGE,"E16.rect.right")])],"isStart":false}),"instanceName":"1"}),"instanceName":"1"});
            var Q16;
            Q16=makeQuery(id+"F17.opPattern","COPY",EDGE,{"derivedFrom":makeQuery(id+"F15.opPattern","COPY",EDGE,{"derivedFrom":makeQuery(id+"F13.opExtrude","CAP_EDGE",EDGE,{"disambiguationData":[OSD([sQuery(id+"F10.wireOp",EDGE,"E28.rect.right")])],"isStart":false}),"instanceName":"1"}),"instanceName":"1"});
            var Q17;
            Q17=makeQuery(id+"F11.opExtrude","CAP_EDGE",EDGE,{"disambiguationData":[OSD([sQuery(id+"F9.wireOp",EDGE,"E16.rect.left")])],"isStart":false});
            var Q18;
            Q18=makeQuery(id+"F11.opExtrude","CAP_EDGE",EDGE,{"disambiguationData":[OSD([sQuery(id+"F9.wireOp",EDGE,"E16.rect.right")])],"isStart":false});
            var Q19;
            Q19=makeQuery(id+"F13.opExtrude","CAP_EDGE",EDGE,{"disambiguationData":[OSD([sQuery(id+"F10.wireOp",EDGE,"E28.rect.left")])],"isStart":false});
            var Q20;
            Q20=makeQuery(id+"F17.opPattern","COPY",EDGE,{"derivedFrom":makeQuery(id+"F15.opPattern","COPY",EDGE,{"derivedFrom":makeQuery(id+"F11.opExtrude","CAP_EDGE",EDGE,{"disambiguationData":[OSD([sQuery(id+"F9.wireOp",EDGE,"E15.rect.bottom")])],"isStart":false}),"instanceName":"1"}),"instanceName":"1"});
            var Q21;
            Q21=makeQuery(id+"F13.opExtrude","CAP_EDGE",EDGE,{"disambiguationData":[OSD([sQuery(id+"F10.wireOp",EDGE,"E27.0")])],"isStart":false});
            var Q22;
            Q22=makeQuery(id+"F11.opExtrude","CAP_EDGE",EDGE,{"disambiguationData":[OSD([sQuery(id+"F9.wireOp",EDGE,"E15.rect.bottom")])],"isStart":false});
            var Q23;
            Q23=makeQuery(id+"F17.opPattern","COPY",EDGE,{"derivedFrom":makeQuery(id+"F15.opPattern","COPY",EDGE,{"derivedFrom":makeQuery(id+"F13.opExtrude","CAP_EDGE",EDGE,{"disambiguationData":[OSD([sQuery(id+"F10.wireOp",EDGE,"E27.0")])],"isStart":false}),"instanceName":"1"}),"instanceName":"1"});
            fillet(context, id + "F21", {"entities" : qUnion([Q0, Q1, Q2, Q3, Q4, Q5, Q6, Q7, Q8, Q9, Q10, Q11, Q12, Q13, Q14, Q15, Q16, Q17, Q18, Q19, Q20, Q21, Q22, Q23]), "radius" : 4 * mm, "tangentPropagation" : true, "allowEdgeOverflow" : false});
        }
        {
            var Q0;
            Q0=makeQuery(id+"F17.opPattern","COPY",EDGE,{"derivedFrom":makeQuery(id+"F15.opPattern","COPY",EDGE,{"derivedFrom":makeQuery(id+"F1.opExtrude","CAP_EDGE",EDGE,{"disambiguationData":[OSD([sQuery(id+"F0.wireOp",EDGE,"E0.rect.bottom")])],"isStart":false}),"instanceName":"1"}),"instanceName":"1"});
            chamfer(context, id + "F22", {"entities" : qUnion([Q0]), "width" : 1 * mm, "tangentPropagation" : true});
        }
        {
            var Q0;
            Q0=makeQuery(id+"F11.opExtrude","CAP_EDGE",EDGE,{"disambiguationData":[OSD([sQuery(id+"F0.wireOp",EDGE,"E1.1"),sQuery(id+"F3.wireOp",EDGE,"E5")])],"isStart":false});
            var Q1;
            Q1=makeQuery(id+"F13.opExtrude","CAP_EDGE",EDGE,{"disambiguationData":[OSD([sQuery(id+"F0.wireOp",EDGE,"E1.2"),sQuery(id+"F6.wireOp",EDGE,"E6")])],"isStart":false});
            var Q2;
            Q2=makeQuery(id+"F17.opPattern","COPY",EDGE,{"derivedFrom":makeQuery(id+"F15.opPattern","COPY",EDGE,{"derivedFrom":makeQuery(id+"F11.opExtrude","CAP_EDGE",EDGE,{"disambiguationData":[OSD([sQuery(id+"F0.wireOp",EDGE,"E1.1"),sQuery(id+"F3.wireOp",EDGE,"E5")])],"isStart":false}),"instanceName":"1"}),"instanceName":"1"});
            var Q3;
            Q3=makeQuery(id+"F17.opPattern","COPY",EDGE,{"derivedFrom":makeQuery(id+"F15.opPattern","COPY",EDGE,{"derivedFrom":makeQuery(id+"F13.opExtrude","CAP_EDGE",EDGE,{"disambiguationData":[OSD([sQuery(id+"F0.wireOp",EDGE,"E1.2"),sQuery(id+"F6.wireOp",EDGE,"E6")])],"isStart":false}),"instanceName":"1"}),"instanceName":"1"});
            fillet(context, id + "F23", {"entities" : qUnion([Q0, Q1, Q2, Q3]), "radius" : 1 * mm, "tangentPropagation" : true, "allowEdgeOverflow" : false});
        }
    });
